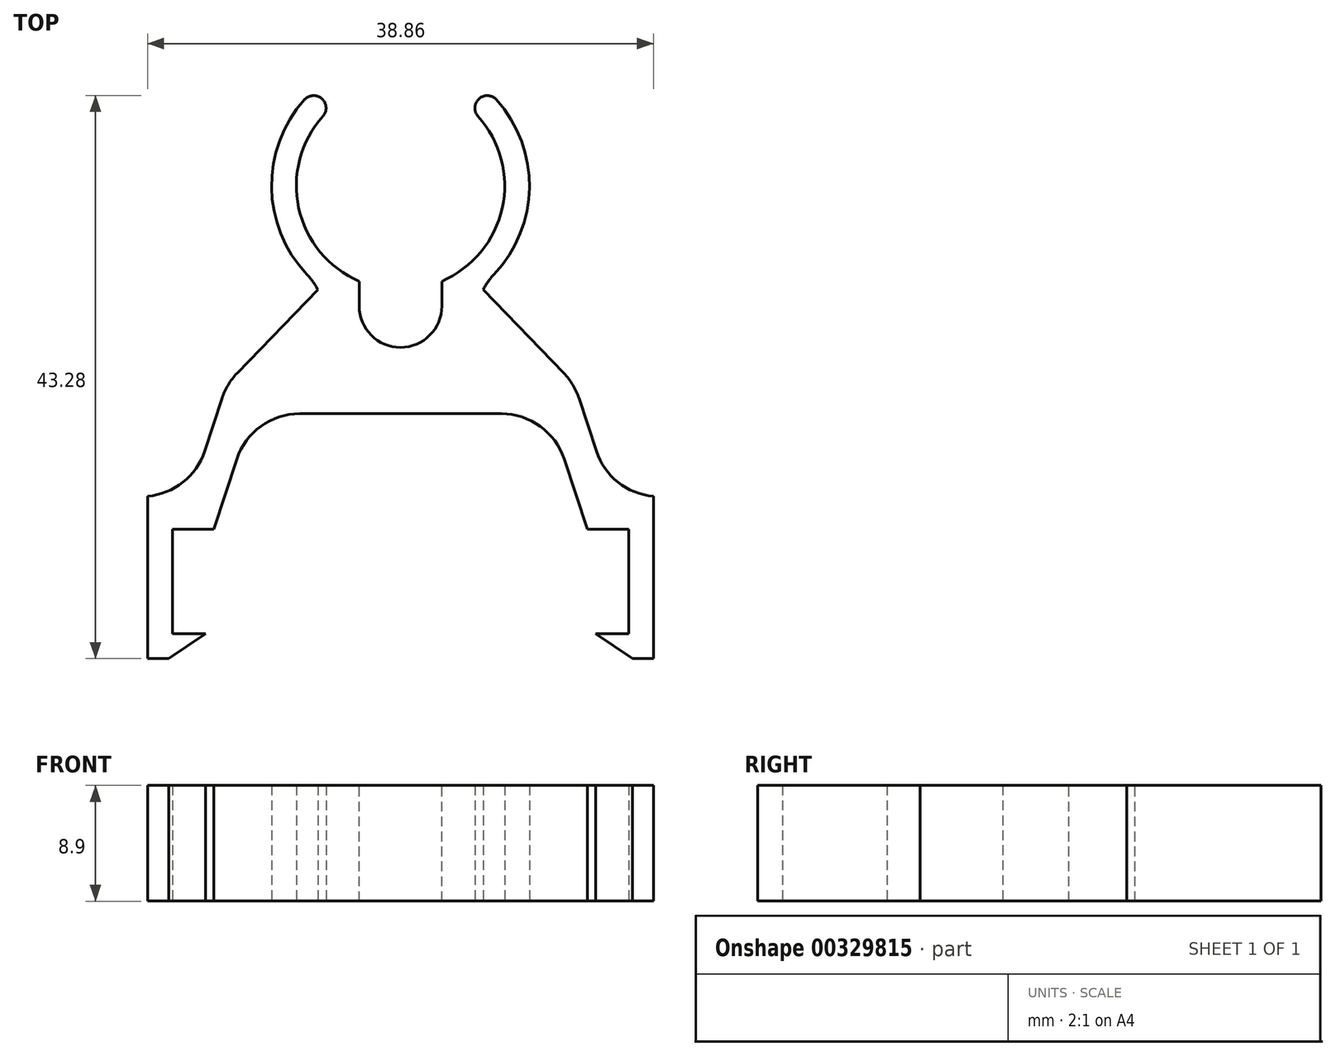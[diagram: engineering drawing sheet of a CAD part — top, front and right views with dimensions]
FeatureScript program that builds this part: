
annotation { "Feature Type Name" : "Feature", "Feature Type Description" : "" }
export const myFeature = defineFeature(function(context is Context, id is Id, definition is map)
    precondition{}
    {
        {
            var Q0;
            Q0=qCreatedBy(makeId("Top.planeOp"),FACE);
            var sketch = newSketch(context, id + "F0", { "sketchPlane" : qUnion([Q0])});
            skArc(sketch, "E0", {"start": v(-5.96, 5.34) * mm, "mid": v(0, -8) * mm, "end": v(5.96, 5.34) * mm});
            skArc(sketch, "E1", {"start": v(-7.38, 6.61) * mm, "mid": v(-9.88, -0.71) * mm, "end": v(-6.35, -7.6) * mm});
            skArc(sketch, "E2", {"start": v(-5.96, 5.34) * mm, "mid": v(-6.03, 6.69) * mm, "end": v(-7.38, 6.61) * mm});
            skArc(sketch, "E3", {"start": v(7.38, 6.61) * mm, "mid": v(6.03, 6.69) * mm, "end": v(5.96, 5.34) * mm});
            skLineSegment(sketch, "E4", {"start": v(-6.35, -7.6) * mm, "end": v(-6.35, -15.62) * mm});
            skLineSegment(sketch, "E5", {"start": v(6.35, -15.62) * mm, "end": v(6.35, -15.62) * mm});
            skLineSegment(sketch, "E6", {"start": v(6.35, -15.62) * mm, "end": v(-6.35, -15.62) * mm});
            skArc(sketch, "E7.trimOffspring", {"start": v(6.35, -7.6) * mm, "mid": v(9.88, -0.71) * mm, "end": v(7.38, 6.61) * mm});
            skLineSegment(sketch, "E8", {"start": v(6.35, -7.6) * mm, "end": v(6.35, -15.62) * mm});
            skLineSegment(sketch, "E9", {"start": v(0, -8) * mm, "end": v(0, -15.62) * mm, "construction": true});
            skSolve(sketch);
        }
        {
            var Q0;
            Q0 = qSketchRegion(id + "F0", true);
            var Q1;
            Q1=makeQuery(id+"F0.imprint","IMPRINT",FACE,{"disambiguationData":[TD([[makeQuery(id+"F0.imprint","IMPRINT",EDGE,{"derivedFrom":sQuery(id+"F0.wireOp",EDGE,"sMBprik8-b5Ds-yZTN-arfg-6G3kgr7FVDsM")}),1.0]])]});
            extrude(context, id + "F1", {"entities" : qUnion([Q0, Q1]), "endBound" : BoundingType.SYMMETRIC, "depth" : 8.9 * mm});
        }
        {
            var Q0;
            Q0=qCreatedBy(makeId("Front.planeOp"),FACE);
            var sketch = newSketch(context, id + "F2", { "sketchPlane" : qUnion([Q0])});
            skCircle(sketch, "E10.cCircle", {"center": v(0, 0) * mm, "radius": 2.86 * mm, "construction": true});
            skLineSegment(sketch, "E10.0", {"start": v(-3.3, 0) * mm, "end": v(-1.65, 2.86) * mm});
            skLineSegment(sketch, "E10.1", {"start": v(-1.65, 2.86) * mm, "end": v(1.65, 2.86) * mm});
            skLineSegment(sketch, "E10.2", {"start": v(1.65, 2.86) * mm, "end": v(3.3, 0) * mm});
            skLineSegment(sketch, "E10.3", {"start": v(3.3, 0) * mm, "end": v(1.65, -2.86) * mm});
            skLineSegment(sketch, "E10.4", {"start": v(1.65, -2.86) * mm, "end": v(-1.65, -2.86) * mm});
            skLineSegment(sketch, "E10.5", {"start": v(-1.65, -2.86) * mm, "end": v(-3.3, 0) * mm});
            skPoint(sketch, "E10.0.midPoint", {"position": v(-2.47, 1.43) * mm});
            skLineSegment(sketch, "E11.0", {"start": v(-2.57, 4.45) * mm, "end": v(2.57, 4.45) * mm});
            skLineSegment(sketch, "E11.1", {"start": v(5.13, 0) * mm, "end": v(2.57, -4.45) * mm});
            skLineSegment(sketch, "E11.2", {"start": v(2.57, -4.45) * mm, "end": v(-2.57, -4.45) * mm});
            skLineSegment(sketch, "E11.3", {"start": v(2.57, 4.44) * mm, "end": v(5.13, 0) * mm});
            skLineSegment(sketch, "E11.4", {"start": v(-2.57, -4.44) * mm, "end": v(-5.13, 0) * mm});
            skLineSegment(sketch, "E11.5", {"start": v(-5.13, 0) * mm, "end": v(-2.57, 4.45) * mm});
            skSolve(sketch);
        }
        {
            var Q0;
            Q0=makeQuery(id+"F1.opExtrude","SWEPT_FACE",FACE,{"disambiguationData":[OSD([sQuery(id+"F0.wireOp",EDGE,"E6")])]});
            var sketch = newSketch(context, id + "F3", { "sketchPlane" : qUnion([Q0])});
            skCircle(sketch, "E12", {"center": v(0, 0) * mm, "radius": 1.6 * mm});
            skSolve(sketch);
        }
        {
            var Q0;
            Q0=qCreatedBy(makeId("Top.planeOp"),FACE);
            var sketch = newSketch(context, id + "F4", { "sketchPlane" : qUnion([Q0])});
            skLineSegment(sketch, "E13", {"start": v(-19.43, -23.88) * mm, "end": v(-19.43, -36.35) * mm});
            skLineSegment(sketch, "E14", {"start": v(-19.43, -36.35) * mm, "end": v(-17.81, -36.35) * mm});
            skLineSegment(sketch, "E15", {"start": v(-17.81, -36.35) * mm, "end": v(-14.99, -34.44) * mm});
            skLineSegment(sketch, "E16", {"start": v(-14.99, -34.44) * mm, "end": v(-17.53, -34.44) * mm});
            skLineSegment(sketch, "E17", {"start": v(-17.53, -34.44) * mm, "end": v(-17.53, -26.42) * mm});
            skLineSegment(sketch, "E18", {"start": v(-17.53, -26.42) * mm, "end": v(-14.35, -26.42) * mm});
            skLineSegment(sketch, "E19.MirrorCS", {"start": v(14.99, -34.44) * mm, "end": v(17.53, -34.44) * mm});
            skLineSegment(sketch, "E20.MirrorCS", {"start": v(19.43, -36.35) * mm, "end": v(17.81, -36.35) * mm});
            skLineSegment(sketch, "E21.MirrorCS", {"start": v(19.43, -23.88) * mm, "end": v(19.43, -36.35) * mm});
            skLineSegment(sketch, "E22.MirrorCS", {"start": v(17.81, -36.35) * mm, "end": v(14.99, -34.44) * mm});
            skLineSegment(sketch, "E23.MirrorCS", {"start": v(17.53, -26.42) * mm, "end": v(14.35, -26.42) * mm});
            skLineSegment(sketch, "E24.MirrorCS", {"start": v(17.53, -34.44) * mm, "end": v(17.53, -26.42) * mm});
            skLineSegment(sketch, "E25", {"start": v(-14.35, -26.42) * mm, "end": v(-11.43, -17.53) * mm});
            skLineSegment(sketch, "E26", {"start": v(-11.43, -17.53) * mm, "end": v(0, -17.53) * mm});
            skLineSegment(sketch, "E27", {"start": v(11.43, -17.53) * mm, "end": v(0, -17.53) * mm});
            skLineSegment(sketch, "E28", {"start": v(14.35, -26.42) * mm, "end": v(11.43, -17.53) * mm});
            skLineSegment(sketch, "E29", {"start": v(-6.35, -8) * mm, "end": v(6.35, -8) * mm});
            skLineSegment(sketch, "E30", {"start": v(-19.43, -23.88) * mm, "end": v(-16.2, -23.88) * mm});
            skLineSegment(sketch, "E31", {"start": v(-16.2, -23.88) * mm, "end": v(-13.35, -15.25) * mm});
            skLineSegment(sketch, "E32", {"start": v(-13.35, -15.25) * mm, "end": v(-6.35, -8) * mm});
            skLineSegment(sketch, "E33", {"start": v(6.35, -8) * mm, "end": v(13.35, -15.25) * mm});
            skLineSegment(sketch, "E34", {"start": v(13.35, -15.25) * mm, "end": v(16.2, -23.88) * mm});
            skLineSegment(sketch, "E35", {"start": v(16.2, -23.88) * mm, "end": v(19.43, -23.88) * mm});
            skLineSegment(sketch, "E36", {"start": v(0, -17.53) * mm, "end": v(0, -8) * mm, "construction": true});
            skSolve(sketch);
        }
        {
            var Q0;
            Q0 = qSketchRegion(id + "F4", true);
            extrude(context, id + "F5", {"entities" : qUnion([Q0]), "operationType" : NewBodyOperationType.ADD, "endBound" : BoundingType.SYMMETRIC, "depth" : 8.9 * mm});
        }
        {
            var Q0;
            Q0=makeQuery(id+"F5.boolean.opBoolean","MERGE",FACE,{"derivedFrom":[makeQuery(id+"F1.opExtrude","CAP_FACE",FACE,{"disambiguationData":[OSD([sQuery(id+"F0.wireOp",EDGE,"E0"),sQuery(id+"F0.wireOp",EDGE,"E1"),sQuery(id+"F0.wireOp",EDGE,"E2"),sQuery(id+"F0.wireOp",EDGE,"E3"),sQuery(id+"F0.wireOp",EDGE,"E4"),sQuery(id+"F0.wireOp",EDGE,"E6"),sQuery(id+"F0.wireOp",EDGE,"E7.trimOffspring"),sQuery(id+"F0.wireOp",EDGE,"E8")])],"isStart":false}),makeQuery(id+"F5.opExtrude","CAP_FACE",FACE,{"disambiguationData":[OSD([sQuery(id+"F4.wireOp",EDGE,"WCUFzmcL-CnK9-h4WN-IlIQ-TFsJAm2cdJFj"),sQuery(id+"F4.wireOp",EDGE,"E13"),sQuery(id+"F4.wireOp",EDGE,"E14"),sQuery(id+"F4.wireOp",EDGE,"E15"),sQuery(id+"F4.wireOp",EDGE,"E16"),sQuery(id+"F4.wireOp",EDGE,"E17"),sQuery(id+"F4.wireOp",EDGE,"E18"),sQuery(id+"F4.wireOp",EDGE,"E19.MirrorCS"),sQuery(id+"F4.wireOp",EDGE,"E20.MirrorCS"),sQuery(id+"F4.wireOp",EDGE,"E21.MirrorCS"),sQuery(id+"F4.wireOp",EDGE,"E22.MirrorCS"),sQuery(id+"F4.wireOp",EDGE,"E23.MirrorCS"),sQuery(id+"F4.wireOp",EDGE,"d97f9cc9-fb89-4b9d-b2e3-22bbbb1108845.MirrorCS"),sQuery(id+"F4.wireOp",EDGE,"E24.MirrorCS")])],"isStart":false})]});
            var sketch = newSketch(context, id + "F6", { "sketchPlane" : qUnion([Q0])});
            skLineSegment(sketch, "E37.bottom", {"start": v(-3.17, -7.34) * mm, "end": v(3.17, -7.34) * mm});
            skLineSegment(sketch, "E37.top", {"start": v(-3.17, -9.25) * mm, "end": v(3.17, -9.25) * mm});
            skLineSegment(sketch, "E37.left", {"start": v(-3.17, -7.34) * mm, "end": v(-3.17, -9.25) * mm});
            skLineSegment(sketch, "E37.right", {"start": v(3.18, -7.34) * mm, "end": v(3.18, -9.25) * mm});
            skLineSegment(sketch, "E38", {"start": v(0, -7.34) * mm, "end": v(0, -9.25) * mm, "construction": true});
            skArc(sketch, "E39", {"start": v(-3.17, -9.25) * mm, "mid": v(0, -12.42) * mm, "end": v(3.17, -9.25) * mm});
            skSolve(sketch);
        }
        {
            var Q0;
            Q0 = qSketchRegion(id + "F6", true);
            extrude(context, id + "F7", {"entities" : qUnion([Q0]), "operationType" : NewBodyOperationType.REMOVE, "endBound" : BoundingType.THROUGH_ALL, "oppositeDirection" : true, "depth" : 25.4 * mm});
        }
        {
            var Q0;
            Q0=makeQuery(id+"F5.opExtrude","SWEPT_EDGE",EDGE,{"disambiguationData":[OSD([sQuery(id+"F4.wireOp",EDGE,"E31"),sQuery(id+"F4.wireOp",EDGE,"E32")])]});
            var Q1;
            Q1=makeQuery(id+"F5.opExtrude","SWEPT_EDGE",EDGE,{"disambiguationData":[OSD([sQuery(id+"F4.wireOp",EDGE,"E33"),sQuery(id+"F4.wireOp",EDGE,"E34")])]});
            var Q2;
            Q2=makeQuery(id+"F5.opExtrude","SWEPT_EDGE",EDGE,{"disambiguationData":[OSD([sQuery(id+"F4.wireOp",EDGE,"E34"),sQuery(id+"F4.wireOp",EDGE,"E35")])]});
            var Q3;
            Q3=makeQuery(id+"F5.opExtrude","SWEPT_EDGE",EDGE,{"disambiguationData":[OSD([sQuery(id+"F4.wireOp",EDGE,"E30"),sQuery(id+"F4.wireOp",EDGE,"E31")])]});
            var Q4;
            Q4=makeQuery(id+"F5.opExtrude","SWEPT_EDGE",EDGE,{"disambiguationData":[OSD([sQuery(id+"F4.wireOp",EDGE,"E29"),sQuery(id+"F4.wireOp",EDGE,"E32")])]});
            var Q5;
            Q5=makeQuery(id+"F5.opExtrude","SWEPT_EDGE",EDGE,{"disambiguationData":[OSD([sQuery(id+"F4.wireOp",EDGE,"E29"),sQuery(id+"F4.wireOp",EDGE,"E33")])]});
            var Q6;
            Q6=makeQuery(id+"F1.opExtrude","SWEPT_EDGE",EDGE,{"disambiguationData":[OSD([sQuery(id+"F0.wireOp",EDGE,"E7.trimOffspring"),sQuery(id+"F0.wireOp",EDGE,"E8")])]});
            var Q7;
            Q7=makeQuery(id+"F1.opExtrude","SWEPT_EDGE",EDGE,{"disambiguationData":[OSD([sQuery(id+"F0.wireOp",EDGE,"E1"),sQuery(id+"F0.wireOp",EDGE,"E4")])]});
            var Q8;
            Q8=makeQuery(id+"F5.opExtrude","SWEPT_EDGE",EDGE,{"disambiguationData":[OSD([sQuery(id+"F4.wireOp",EDGE,"E25"),sQuery(id+"F4.wireOp",EDGE,"E26")])]});
            var Q9;
            Q9=makeQuery(id+"F5.opExtrude","SWEPT_EDGE",EDGE,{"disambiguationData":[OSD([sQuery(id+"F4.wireOp",EDGE,"E27"),sQuery(id+"F4.wireOp",EDGE,"E28")])]});
            fillet(context, id + "F8", {"entities" : qUnion([Q0, Q1, Q2, Q3, Q4, Q5, Q6, Q7, Q8, Q9]), "radius" : 5.08 * mm, "tangentPropagation" : true, "allowEdgeOverflow" : false});
        }
    });
